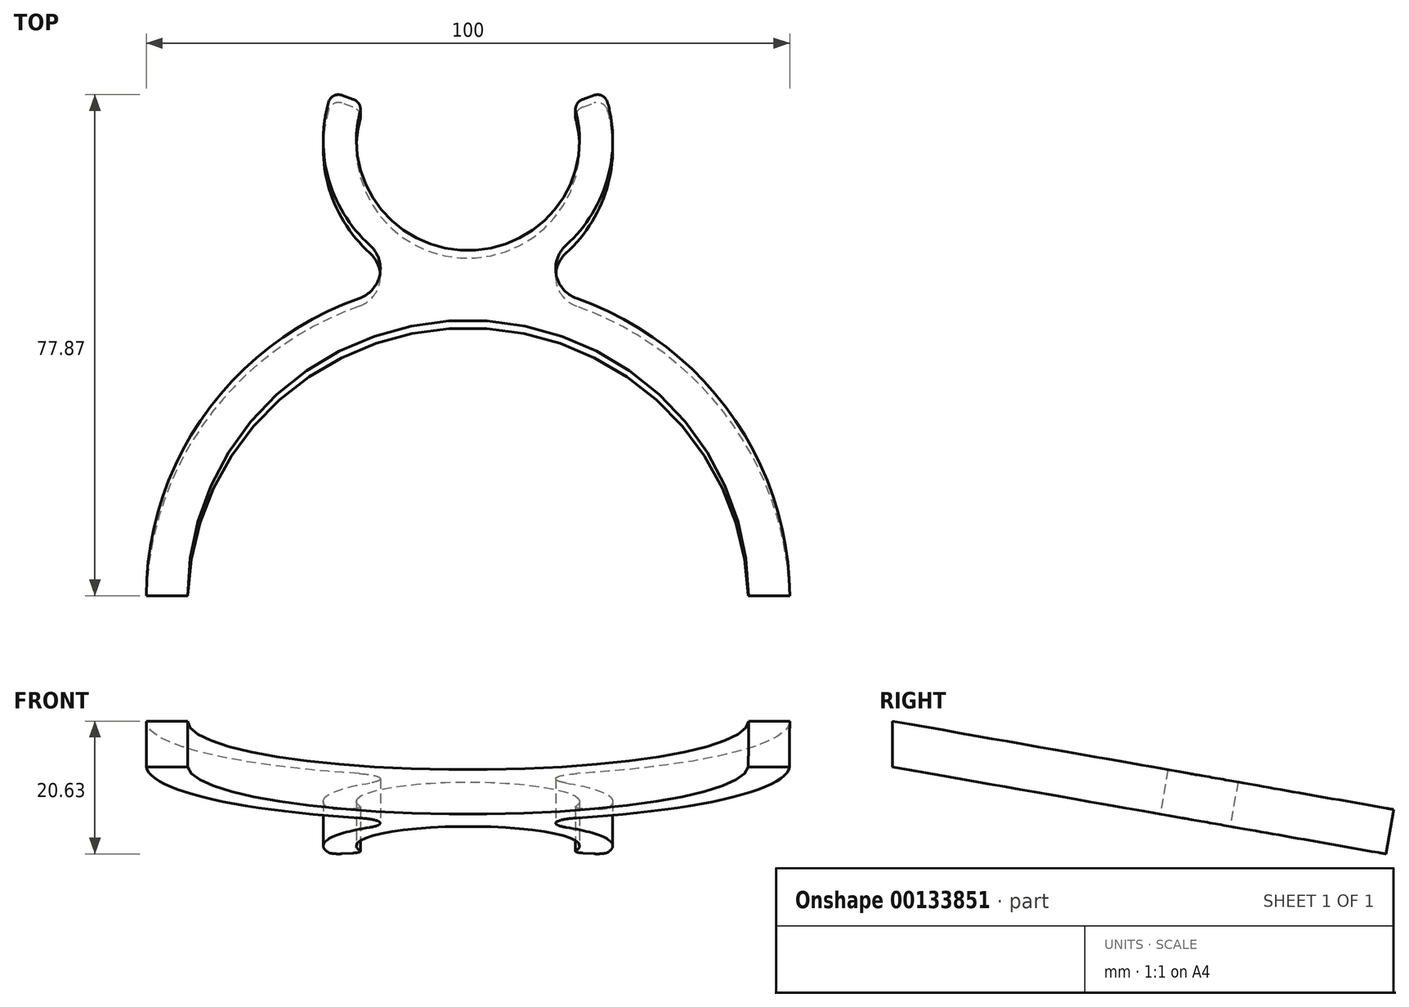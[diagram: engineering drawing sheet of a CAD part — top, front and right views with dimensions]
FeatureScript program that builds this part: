
annotation { "Feature Type Name" : "Feature", "Feature Type Description" : "" }
export const myFeature = defineFeature(function(context is Context, id is Id, definition is map)
    precondition{}
    {
        {
            var Q0;
            Q0=qCreatedBy(makeId("Top.planeOp"),FACE);
            var sketch = newSketch(context, id + "F0", { "sketchPlane" : qUnion([Q0])});
            skArc(sketch, "E0", {"start": v(-16.77, 4.46) * mm, "mid": v(0, -17.35) * mm, "end": v(16.77, 4.46) * mm});
            skArc(sketch, "E1", {"start": v(50, -71.99) * mm, "mid": v(40.9, -43.23) * mm, "end": v(16.93, -24.94) * mm});
            skArc(sketch, "E2", {"start": v(15.24, -16.56) * mm, "mid": v(21.64, -6.16) * mm, "end": v(21.67, 6.05) * mm});
            skLineSegment(sketch, "E3", {"start": v(-17.83, 6.49) * mm, "end": v(-19.58, 7.13) * mm});
            skLineSegment(sketch, "E4.MirrorCS", {"start": v(17.83, 6.49) * mm, "end": v(19.58, 7.13) * mm});
            skArc(sketch, "E5", {"start": v(43.6, -71.99) * mm, "mid": v(0, -28.39) * mm, "end": v(-43.6, -71.99) * mm});
            skLineSegment(sketch, "E6", {"start": v(-50, -71.99) * mm, "end": v(-43.6, -71.99) * mm});
            skLineSegment(sketch, "E7.trimOffspring", {"start": v(43.6, -71.99) * mm, "end": v(50, -71.99) * mm});
            skPoint(sketch, "E8.orphan", {"position": v(-58.4, -71.99) * mm});
            skArc(sketch, "E9.trimOffspring", {"start": v(-16.93, -24.94) * mm, "mid": v(-40.9, -43.23) * mm, "end": v(-50, -71.99) * mm});
            skArc(sketch, "E10.trimOffspring", {"start": v(-21.67, 6.05) * mm, "mid": v(-21.64, -6.16) * mm, "end": v(-15.24, -16.56) * mm});
            skPoint(sketch, "E11.orphan", {"position": v(-30.32, 11.04) * mm});
            skPoint(sketch, "E12.orphan", {"position": v(30.32, 11.04) * mm});
            skPoint(sketch, "E13.visualSharp", {"position": v(-3.97, -22.15) * mm});
            skArc(sketch, "E13.filletArc", {"start": v(-16.93, -24.94) * mm, "mid": v(-13.72, -21.23) * mm, "end": v(-15.24, -16.56) * mm});
            skPoint(sketch, "E14.visualSharp", {"position": v(3.97, -22.15) * mm});
            skArc(sketch, "E14.filletArc", {"start": v(15.24, -16.56) * mm, "mid": v(13.72, -21.23) * mm, "end": v(16.93, -24.94) * mm});
            skPoint(sketch, "E15.visualSharp", {"position": v(-21.14, 7.7) * mm});
            skArc(sketch, "E15.filletArc", {"start": v(-19.58, 7.13) * mm, "mid": v(-20.86, 7.05) * mm, "end": v(-21.67, 6.05) * mm});
            skPoint(sketch, "E16.visualSharp", {"position": v(-16.3, 5.93) * mm});
            skArc(sketch, "E16.filletArc", {"start": v(-16.77, 4.46) * mm, "mid": v(-16.9, 5.68) * mm, "end": v(-17.83, 6.49) * mm});
            skPoint(sketch, "E17.visualSharp", {"position": v(16.3, 5.93) * mm});
            skArc(sketch, "E17.filletArc", {"start": v(17.83, 6.49) * mm, "mid": v(16.9, 5.68) * mm, "end": v(16.77, 4.46) * mm});
            skPoint(sketch, "E18.visualSharp", {"position": v(21.14, 7.7) * mm});
            skArc(sketch, "E18.filletArc", {"start": v(21.67, 6.05) * mm, "mid": v(20.86, 7.05) * mm, "end": v(19.58, 7.13) * mm});
            skSolve(sketch);
        }
        {
            var Q0;
            Q0=makeQuery(id+"F0.imprint","IMPRINT",FACE,{"disambiguationData":[TD([[makeQuery(id+"F0.imprint","IMPRINT",EDGE,{"derivedFrom":sQuery(id+"F0.wireOp",EDGE,"E0")}),-1.0]])]});
            extrude(context, id + "F1", {"entities" : qUnion([Q0]), "depth" : 7 * mm});
        }
        {
            var Q0;
            Q0=makeQuery(id+"F1.opExtrude","SWEPT_BODY",BODY,{"disambiguationData":[OSD([sQuery(id+"F0.wireOp",EDGE,"E0"),sQuery(id+"F0.wireOp",EDGE,"E1"),sQuery(id+"F0.wireOp",EDGE,"E2"),sQuery(id+"F0.wireOp",EDGE,"E3"),sQuery(id+"F0.wireOp",EDGE,"E4.MirrorCS"),sQuery(id+"F0.wireOp",EDGE,"E5"),sQuery(id+"F0.wireOp",EDGE,"E6"),sQuery(id+"F0.wireOp",EDGE,"E7.trimOffspring"),sQuery(id+"F0.wireOp",EDGE,"E9.trimOffspring"),sQuery(id+"F0.wireOp",EDGE,"E10.trimOffspring"),sQuery(id+"F0.wireOp",EDGE,"E13.filletArc"),sQuery(id+"F0.wireOp",EDGE,"E14.filletArc"),sQuery(id+"F0.wireOp",EDGE,"E15.filletArc"),sQuery(id+"F0.wireOp",EDGE,"E16.filletArc"),sQuery(id+"F0.wireOp",EDGE,"E17.filletArc"),sQuery(id+"F0.wireOp",EDGE,"E18.filletArc")])]});
            var Q1;
            Q1=makeQuery(id+"F1.opExtrude","CAP_EDGE",EDGE,{"disambiguationData":[OSD([sQuery(id+"F0.wireOp",EDGE,"E6")])],"isStart":false});
            transform(context, id + "F2", {"entities" : qUnion([Q0]), "transformType" : TransformType.ROTATION, "transformAxis" : qUnion([Q1]), "angle" : 10 * degree, "oppositeDirection" : true, "makeCopy" : false});
        }
        {
            var Q0;
            Q0=qCreatedBy(makeId("Front.planeOp"),FACE);
            var sketch = newSketch(context, id + "F3", { "sketchPlane" : qUnion([Q0])});
            skLineSegment(sketch, "E19.bottom", {"start": v(61.46, 34.34) * mm, "end": v(-64.95, 34.34) * mm});
            skLineSegment(sketch, "E19.top", {"start": v(61.46, -28.31) * mm, "end": v(-64.95, -28.31) * mm});
            skLineSegment(sketch, "E19.left", {"start": v(61.46, 34.34) * mm, "end": v(61.46, -28.31) * mm});
            skLineSegment(sketch, "E19.right", {"start": v(-64.95, 34.34) * mm, "end": v(-64.95, -28.31) * mm});
            skSolve(sketch);
        }
        {
            var Q0;
            Q0=makeQuery(id+"F3.imprint","IMPRINT",FACE,{"disambiguationData":[TD([[makeQuery(id+"F3.imprint","IMPRINT",EDGE,{"derivedFrom":sQuery(id+"F3.wireOp",EDGE,"E19.bottom")}),1.0]])]});
            extrude(context, id + "F4", {"entities" : qUnion([Q0]), "depth" : 25 * mm});
        }
        {
            var Q0;
            Q0=makeQuery(id+"F4.opExtrude","SWEPT_BODY",BODY,{"disambiguationData":[OSD([sQuery(id+"F3.wireOp",EDGE,"E19.bottom"),sQuery(id+"F3.wireOp",EDGE,"E19.top"),sQuery(id+"F3.wireOp",EDGE,"E19.left"),sQuery(id+"F3.wireOp",EDGE,"E19.right")])]});
            transform(context, id + "F5", {"entities" : qUnion([Q0]), "transformType" : TransformType.TRANSLATION_3D, "dx" : 0 * mm, "dy" : -71.85 * mm, "dz" : 0 * mm, "makeCopy" : false});
        }
        {
            var Q0;
            Q0=makeQuery(id+"F4.opExtrude","SWEPT_BODY",BODY,{"disambiguationData":[OSD([sQuery(id+"F3.wireOp",EDGE,"E19.bottom"),sQuery(id+"F3.wireOp",EDGE,"E19.top"),sQuery(id+"F3.wireOp",EDGE,"E19.left"),sQuery(id+"F3.wireOp",EDGE,"E19.right")])]});
            var Q1;
            Q1=makeQuery(id+"F1.opExtrude","SWEPT_BODY",BODY,{"disambiguationData":[OSD([sQuery(id+"F0.wireOp",EDGE,"E0"),sQuery(id+"F0.wireOp",EDGE,"E1"),sQuery(id+"F0.wireOp",EDGE,"E2"),sQuery(id+"F0.wireOp",EDGE,"E3"),sQuery(id+"F0.wireOp",EDGE,"E4.MirrorCS"),sQuery(id+"F0.wireOp",EDGE,"E5"),sQuery(id+"F0.wireOp",EDGE,"E6"),sQuery(id+"F0.wireOp",EDGE,"E7.trimOffspring"),sQuery(id+"F0.wireOp",EDGE,"E9.trimOffspring"),sQuery(id+"F0.wireOp",EDGE,"E10.trimOffspring"),sQuery(id+"F0.wireOp",EDGE,"E13.filletArc"),sQuery(id+"F0.wireOp",EDGE,"E14.filletArc"),sQuery(id+"F0.wireOp",EDGE,"E15.filletArc"),sQuery(id+"F0.wireOp",EDGE,"E16.filletArc"),sQuery(id+"F0.wireOp",EDGE,"E17.filletArc"),sQuery(id+"F0.wireOp",EDGE,"E18.filletArc")])]});
            booleanBodies(context, id + "F6", {"operationType" : BooleanOperationType.SUBTRACTION, "tools" : qUnion([Q0]), "targets" : qUnion([Q1])});
        }
    });
